annotation { "Feature Type Name" : "Feature", "Feature Type Description" : "" }
export const myFeature = defineFeature(function(context is Context, id is Id, definition is map)
    precondition{}
    {
        {
            var Q0;
            Q0=qCreatedBy(makeId("Front.planeOp"),FACE);
            var sketch = newSketch(context, id + "F0", { "sketchPlane" : qUnion([Q0])});
            skPoint(sketch, "E0", {"position": v(0, 50) * mm});
            skPoint(sketch, "E1.0.midPoint", {"position": v(0, 5) * mm});
            skLineSegment(sketch, "E2", {"start": v(-52.9, 67.19) * mm, "end": v(-12.49, 67.19) * mm});
            skLineSegment(sketch, "E3", {"start": v(52.9, 67.19) * mm, "end": v(20.2, 43.43) * mm});
            skLineSegment(sketch, "E4", {"start": v(-31.51, 8.63) * mm, "end": v(-20.2, 43.43) * mm});
            skLineSegment(sketch, "E5", {"start": v(0, 105.62) * mm, "end": v(12.49, 67.19) * mm});
            skLineSegment(sketch, "E6", {"start": v(27.7, 8.63) * mm, "end": v(0, 28.75) * mm});
            skLineSegment(sketch, "E7.trimOffspring", {"start": v(12.49, 67.19) * mm, "end": v(52.9, 67.19) * mm});
            skLineSegment(sketch, "E8.trimOffspring", {"start": v(-12.49, 67.19) * mm, "end": v(0, 105.62) * mm});
            skLineSegment(sketch, "E9.trimOffspring", {"start": v(20.2, 43.43) * mm, "end": v(31.51, 8.63) * mm});
            skLineSegment(sketch, "E10.trimOffspring", {"start": v(0, 28.75) * mm, "end": v(-27.7, 8.63) * mm});
            skLineSegment(sketch, "E11.trimOffspring", {"start": v(-20.2, 43.43) * mm, "end": v(-52.9, 67.19) * mm});
            skLineSegment(sketch, "E12.0", {"start": v(-34.43, 61.19) * mm, "end": v(-8.13, 61.19) * mm});
            skLineSegment(sketch, "E12.1", {"start": v(-13.15, 45.73) * mm, "end": v(-34.43, 61.19) * mm});
            skLineSegment(sketch, "E12.2", {"start": v(-8.13, 61.19) * mm, "end": v(0, 86.2) * mm});
            skLineSegment(sketch, "E12.3", {"start": v(-21.28, 20.7) * mm, "end": v(-13.15, 45.73) * mm});
            skLineSegment(sketch, "E12.4", {"start": v(0, 36.17) * mm, "end": v(-21.28, 20.7) * mm});
            skLineSegment(sketch, "E12.5", {"start": v(21.28, 20.7) * mm, "end": v(0, 36.17) * mm});
            skLineSegment(sketch, "E12.6", {"start": v(0, 86.2) * mm, "end": v(8.13, 61.19) * mm});
            skLineSegment(sketch, "E12.7", {"start": v(8.13, 61.19) * mm, "end": v(34.43, 61.19) * mm});
            skLineSegment(sketch, "E12.8", {"start": v(34.43, 61.19) * mm, "end": v(13.15, 45.73) * mm});
            skLineSegment(sketch, "E12.9", {"start": v(13.15, 45.73) * mm, "end": v(21.28, 20.7) * mm});
            skLineSegment(sketch, "E13", {"start": v(-27.7, 8.63) * mm, "end": v(-31.51, 8.63) * mm});
            skLineSegment(sketch, "E14", {"start": v(27.7, 8.63) * mm, "end": v(31.51, 8.63) * mm});
            skPoint(sketch, "E15.start.orphan", {"position": v(32.7, 5) * mm});
            skPoint(sketch, "E1.0.end.orphan", {"position": v(-32.7, 5) * mm});
            skSolve(sketch);
        }
        {
            var Q0;
            Q0=makeQuery(id+"F0.imprint","IMPRINT",FACE,{"disambiguationData":[TD([[makeQuery(id+"F0.imprint","IMPRINT",EDGE,{"derivedFrom":sQuery(id+"F0.wireOp",EDGE,"E2")}),-1.0]])]});
            extrude(context, id + "F1", {"entities" : qUnion([Q0]), "depth" : 20 * mm});
        }
        {
            var Q0;
            Q0=makeQuery(id+"F1.opExtrude","SWEPT_EDGE",EDGE,{"disambiguationData":[OSD([sQuery(id+"F0.wireOp",EDGE,"E5"),sQuery(id+"F0.wireOp",EDGE,"E8.trimOffspring")])]});
            var Q1;
            Q1=makeQuery(id+"F1.opExtrude","SWEPT_EDGE",EDGE,{"disambiguationData":[OSD([sQuery(id+"F0.wireOp",EDGE,"E2"),sQuery(id+"F0.wireOp",EDGE,"E11.trimOffspring")])]});
            var Q2;
            Q2=makeQuery(id+"F1.opExtrude","SWEPT_EDGE",EDGE,{"disambiguationData":[OSD([sQuery(id+"F0.wireOp",EDGE,"E3"),sQuery(id+"F0.wireOp",EDGE,"E7.trimOffspring")])]});
            fillet(context, id + "F2", {"entities" : qUnion([Q0, Q1, Q2]), "radius" : 3 * mm, "tangentPropagation" : true, "allowEdgeOverflow" : false});
        }
        {
            var Q0;
            Q0=qCreatedBy(makeId("Right.planeOp"),FACE);
            var sketch = newSketch(context, id + "F3", { "sketchPlane" : qUnion([Q0])});
            skLineSegment(sketch, "E16.0", {"start": v(-20, 8.63) * mm, "end": v(0, 8.63) * mm});
            skLineSegment(sketch, "E17", {"start": v(0, 8.63) * mm, "end": v(0, -1.37) * mm});
            skLineSegment(sketch, "E18", {"start": v(-20, 8.63) * mm, "end": v(-35, 8.63) * mm});
            skLineSegment(sketch, "E19", {"start": v(0, -1.37) * mm, "end": v(-40, -1.37) * mm});
            skLineSegment(sketch, "E20", {"start": v(-40, -1.37) * mm, "end": v(-35, 8.63) * mm});
            skSolve(sketch);
        }
        {
            var Q0;
            Q0=makeQuery(id+"F3.imprint","IMPRINT",FACE,{"disambiguationData":[TD([[makeQuery(id+"F3.imprint","IMPRINT",EDGE,{"derivedFrom":sQuery(id+"F3.wireOp",EDGE,"E16.0")}),-1.0]])]});
            extrude(context, id + "F4", {"entities" : qUnion([Q0]), "operationType" : NewBodyOperationType.ADD, "depth" : 35 * mm});
        }
        {
            var Q0;
            Q0=makeQuery(id+"F4.opExtrude","CAP_FACE",FACE,{"disambiguationData":[OSD([sQuery(id+"F3.wireOp",EDGE,"E16.0"),sQuery(id+"F3.wireOp",EDGE,"E17"),sQuery(id+"F3.wireOp",EDGE,"E18"),sQuery(id+"F3.wireOp",EDGE,"E19"),sQuery(id+"F3.wireOp",EDGE,"E20")])],"isStart":true});
            extrude(context, id + "F5", {"entities" : qUnion([Q0]), "operationType" : NewBodyOperationType.ADD, "depth" : 35 * mm});
        }
        {
            var Q0;
            {var subQ0=sQuery(id+"F3.wireOp",EDGE,"E20");Q0=makeQuery(id+"F5.boolean.opBoolean","MERGE",FACE,{"derivedFrom":[makeQuery(id+"F4.opExtrude","SWEPT_FACE",FACE,{"disambiguationData":[OSD([subQ0])]}),makeQuery(id+"F5.opExtrude","SWEPT_FACE",FACE,{"disambiguationData":[OSD([subQ0])]})]});}
            var sketch = newSketch(context, id + "F6", { "sketchPlane" : qUnion([Q0])});
            skText(sketch, "E21", { "text": "Best Teacher Award", "fontName": "OpenSans-Bold.ttf"});
            skText(sketch, "E22", { "text": "Miss Paterson", "fontName": "OpenSans-Bold.ttf"});
            skPoint(sketch, "E23", {"position": v(0, -19.11) * mm});
            const initialGuessF6  = {"E21": [-0.0343, -0.01328, 1, 0, 0.00493], "E22": [-0.02, -0.01852, 1, 0, 0.00413]};
            skSetInitialGuess(sketch, initialGuessF6);
            skSolve(sketch);
        }
        {
            var Q0;
            Q0 = qSketchRegion(id + "F6", true);
            extrude(context, id + "F7", {"entities" : qUnion([Q0]), "operationType" : NewBodyOperationType.ADD, "depth" : 1 * mm});
        }
    });